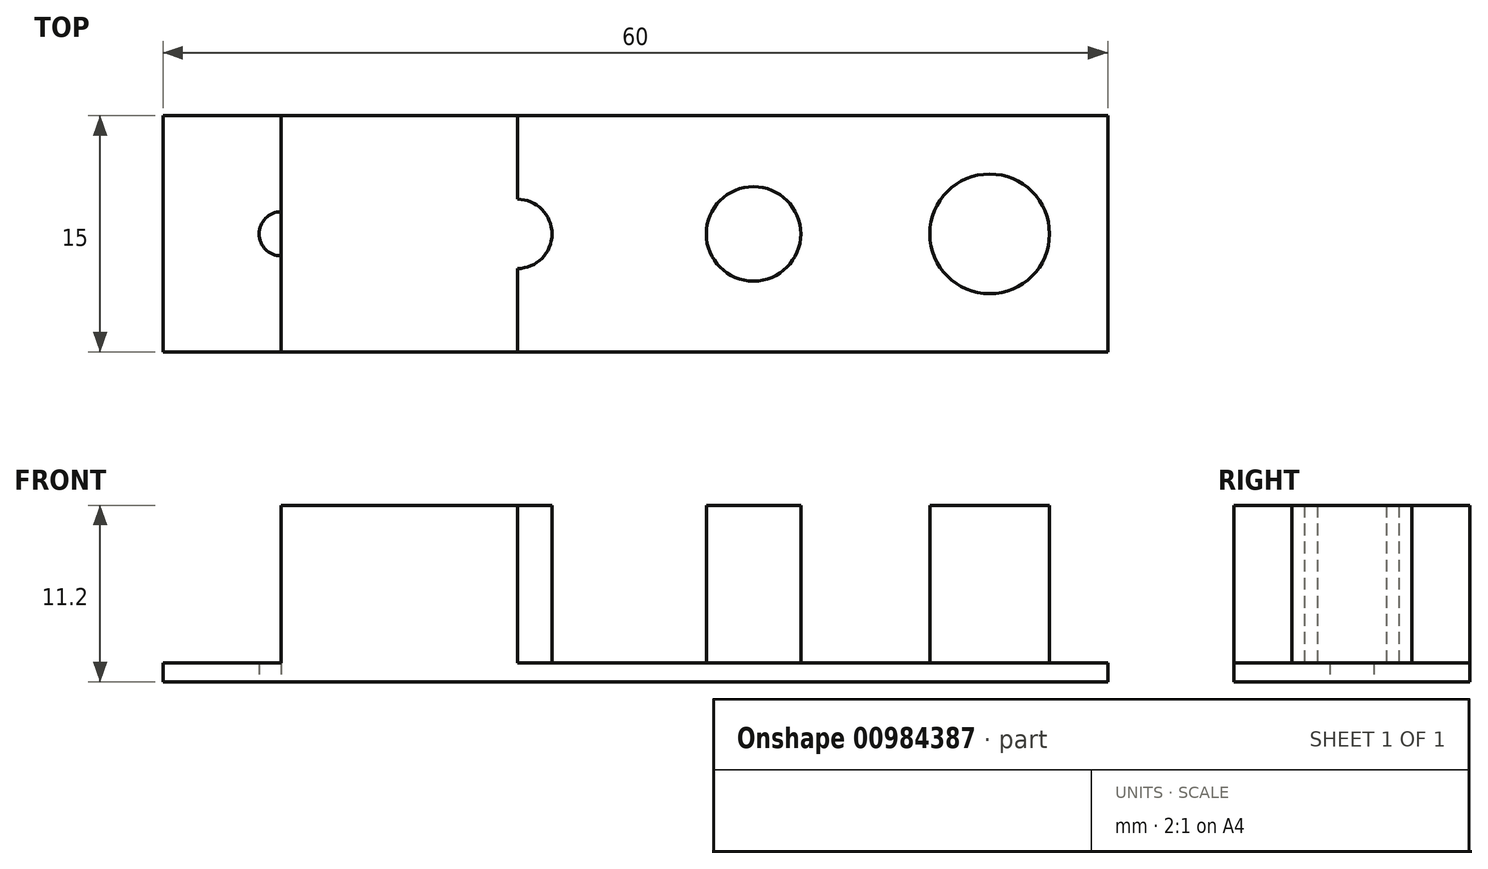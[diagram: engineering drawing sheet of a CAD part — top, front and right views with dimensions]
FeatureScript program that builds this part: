
annotation { "Feature Type Name" : "Feature", "Feature Type Description" : "" }
export const myFeature = defineFeature(function(context is Context, id is Id, definition is map)
    precondition{}
    {
        {
            var Q0;
            Q0=qCreatedBy(makeId("Top.planeOp"),FACE);
            var sketch = newSketch(context, id + "F0", { "sketchPlane" : qUnion([Q0])});
            skLineSegment(sketch, "E0.bottom", {"start": v(0, 0) * mm, "end": v(60, 0) * mm});
            skLineSegment(sketch, "E0.top", {"start": v(0, -15) * mm, "end": v(60, -15) * mm});
            skLineSegment(sketch, "E0.left", {"start": v(0, 0) * mm, "end": v(0, -15) * mm});
            skLineSegment(sketch, "E0.right", {"start": v(60, 0) * mm, "end": v(60, -15) * mm});
            skLineSegment(sketch, "E1.0", {"start": v(0, -7.5) * mm, "end": v(60, -7.5) * mm});
            skLineSegment(sketch, "E2.0", {"start": v(7.5, 0) * mm, "end": v(7.5, -30) * mm});
            skLineSegment(sketch, "E3.0", {"start": v(22.5, 0) * mm, "end": v(22.5, -30) * mm});
            skLineSegment(sketch, "E4.0", {"start": v(37.5, 0) * mm, "end": v(37.5, -30) * mm});
            skLineSegment(sketch, "E5.0", {"start": v(52.5, 0) * mm, "end": v(52.5, -30) * mm});
            skCircle(sketch, "E6", {"center": v(7.5, -7.5) * mm, "radius": 1.4 * mm});
            skCircle(sketch, "E7", {"center": v(22.5, -7.5) * mm, "radius": 2.2 * mm});
            skCircle(sketch, "E8", {"center": v(52.5, -7.5) * mm, "radius": 3.8 * mm});
            skCircle(sketch, "E9", {"center": v(37.5, -7.5) * mm, "radius": 3 * mm});
            skSolve(sketch);
        }
        {
            var Q0;
            {var subQ1=sQuery(id+"F0.wireOp",EDGE,"E0.bottom");var subQ6=sQuery(id+"F0.wireOp",EDGE,"E0.left");var subQ9=makeQuery(id+"F0.imprint","INTERSECT",VERTEX,{"derivedFrom":[subQ1,subQ6]});Q0=makeQuery(id+"F0.imprint","IMPRINT",FACE,{"disambiguationData":[TD([[makeQuery(id+"F0.imprint","IMPRINT",EDGE,{"disambiguationData":[TD([[subQ9,-1.0]])],"derivedFrom":subQ1}),-1.0]])]});}
            var Q1;
            {var subQ1=sQuery(id+"F0.wireOp",EDGE,"E0.left");var subQ5=sQuery(id+"F0.wireOp",EDGE,"E0.top");var subQ6=makeQuery(id+"F0.imprint","INTERSECT",VERTEX,{"derivedFrom":[subQ5,subQ1]});Q1=makeQuery(id+"F0.imprint","IMPRINT",FACE,{"disambiguationData":[TD([[makeQuery(id+"F0.imprint","IMPRINT",EDGE,{"disambiguationData":[TD([[subQ6,-1.0]])],"derivedFrom":subQ5}),1.0]])]});}
            var Q2;
            {var subQ1=sQuery(id+"F0.wireOp",EDGE,"E0.top");var subQ5=sQuery(id+"F0.wireOp",EDGE,"E2.0");var subQ6=makeQuery(id+"F0.imprint","INTERSECT",VERTEX,{"derivedFrom":[subQ1,subQ5]});Q2=makeQuery(id+"F0.imprint","IMPRINT",FACE,{"disambiguationData":[TD([[makeQuery(id+"F0.imprint","IMPRINT",EDGE,{"disambiguationData":[TD([[subQ6,-1.0]])],"derivedFrom":subQ1}),1.0]])]});}
            var Q3;
            {var subQ0=sQuery(id+"F0.wireOp",EDGE,"E2.0");var subQ1=sQuery(id+"F0.wireOp",EDGE,"E0.bottom");var subQ2=makeQuery(id+"F0.imprint","INTERSECT",VERTEX,{"derivedFrom":[subQ1,subQ0]});Q3=makeQuery(id+"F0.imprint","IMPRINT",FACE,{"disambiguationData":[TD([[makeQuery(id+"F0.imprint","IMPRINT",EDGE,{"disambiguationData":[TD([[subQ2,-1.0]])],"derivedFrom":subQ1}),-1.0]])]});}
            var Q4;
            {var subQ0=sQuery(id+"F0.wireOp",EDGE,"E3.0");var subQ1=sQuery(id+"F0.wireOp",EDGE,"E0.bottom");var subQ2=makeQuery(id+"F0.imprint","INTERSECT",VERTEX,{"derivedFrom":[subQ1,subQ0]});Q4=makeQuery(id+"F0.imprint","IMPRINT",FACE,{"disambiguationData":[TD([[makeQuery(id+"F0.imprint","IMPRINT",EDGE,{"disambiguationData":[TD([[subQ2,-1.0]])],"derivedFrom":subQ1}),-1.0]])]});}
            var Q5;
            {var subQ1=sQuery(id+"F0.wireOp",EDGE,"E0.top");var subQ5=sQuery(id+"F0.wireOp",EDGE,"E3.0");var subQ6=makeQuery(id+"F0.imprint","INTERSECT",VERTEX,{"derivedFrom":[subQ1,subQ5]});Q5=makeQuery(id+"F0.imprint","IMPRINT",FACE,{"disambiguationData":[TD([[makeQuery(id+"F0.imprint","IMPRINT",EDGE,{"disambiguationData":[TD([[subQ6,-1.0]])],"derivedFrom":subQ1}),1.0]])]});}
            var Q6;
            {var subQ1=sQuery(id+"F0.wireOp",EDGE,"E0.top");var subQ7=sQuery(id+"F0.wireOp",EDGE,"E4.0");var subQ8=makeQuery(id+"F0.imprint","INTERSECT",VERTEX,{"derivedFrom":[subQ1,subQ7]});Q6=makeQuery(id+"F0.imprint","IMPRINT",FACE,{"disambiguationData":[TD([[makeQuery(id+"F0.imprint","IMPRINT",EDGE,{"disambiguationData":[TD([[subQ8,-1.0]])],"derivedFrom":subQ1}),1.0]])]});}
            var Q7;
            {var subQ1=sQuery(id+"F0.wireOp",EDGE,"E0.bottom");var subQ5=sQuery(id+"F0.wireOp",EDGE,"E4.0");var subQ6=makeQuery(id+"F0.imprint","INTERSECT",VERTEX,{"derivedFrom":[subQ1,subQ5]});Q7=makeQuery(id+"F0.imprint","IMPRINT",FACE,{"disambiguationData":[TD([[makeQuery(id+"F0.imprint","IMPRINT",EDGE,{"disambiguationData":[TD([[subQ6,-1.0]])],"derivedFrom":subQ1}),-1.0]])]});}
            var Q8;
            {var subQ1=sQuery(id+"F0.wireOp",EDGE,"E0.right");var subQ5=sQuery(id+"F0.wireOp",EDGE,"E0.bottom");var subQ6=makeQuery(id+"F0.imprint","INTERSECT",VERTEX,{"derivedFrom":[subQ5,subQ1]});Q8=makeQuery(id+"F0.imprint","IMPRINT",FACE,{"disambiguationData":[TD([[makeQuery(id+"F0.imprint","IMPRINT",EDGE,{"disambiguationData":[TD([[subQ6,1.0]])],"derivedFrom":subQ5}),-1.0]])]});}
            var Q9;
            {var subQ1=sQuery(id+"F0.wireOp",EDGE,"E0.top");var subQ5=sQuery(id+"F0.wireOp",EDGE,"E0.right");var subQ6=makeQuery(id+"F0.imprint","INTERSECT",VERTEX,{"derivedFrom":[subQ1,subQ5]});Q9=makeQuery(id+"F0.imprint","IMPRINT",FACE,{"disambiguationData":[TD([[makeQuery(id+"F0.imprint","IMPRINT",EDGE,{"disambiguationData":[TD([[subQ6,1.0]])],"derivedFrom":subQ1}),1.0]])]});}
            extrude(context, id + "F1", {"entities" : qUnion([Q0, Q1, Q2, Q3, Q4, Q5, Q6, Q7, Q8, Q9]), "depth" : 1.2 * mm, "offsetDistance" : 25 * mm});
        }
        {
            var Q0;
            {var subQ0=sQuery(id+"F0.wireOp",EDGE,"E6");var subQ1=sQuery(id+"F0.wireOp",EDGE,"E1.0");var subQ2=makeQuery(id+"F0.imprint","INTERSECT",VERTEX,{"disambiguationData":[OD(0.0)],"derivedFrom":[subQ1,subQ0]});Q0=makeQuery(id+"F0.imprint","IMPRINT",FACE,{"disambiguationData":[TD([[makeQuery(id+"F0.imprint","IMPRINT",EDGE,{"disambiguationData":[TD([[subQ2,-1.0]])],"derivedFrom":subQ1}),1.0]])]});}
            var Q1;
            {var subQ0=sQuery(id+"F0.wireOp",EDGE,"E2.0");var subQ1=sQuery(id+"F0.wireOp",EDGE,"E1.0");var subQ2=makeQuery(id+"F0.imprint","INTERSECT",VERTEX,{"derivedFrom":[subQ1,subQ0]});Q1=makeQuery(id+"F0.imprint","IMPRINT",FACE,{"disambiguationData":[TD([[makeQuery(id+"F0.imprint","IMPRINT",EDGE,{"disambiguationData":[TD([[subQ2,-1.0]])],"derivedFrom":subQ1}),1.0]])]});}
            var Q2;
            {var subQ0=sQuery(id+"F0.wireOp",EDGE,"E2.0");var subQ1=sQuery(id+"F0.wireOp",EDGE,"E1.0");var subQ2=makeQuery(id+"F0.imprint","INTERSECT",VERTEX,{"derivedFrom":[subQ1,subQ0]});Q2=makeQuery(id+"F0.imprint","IMPRINT",FACE,{"disambiguationData":[TD([[makeQuery(id+"F0.imprint","IMPRINT",EDGE,{"disambiguationData":[TD([[subQ2,-1.0]])],"derivedFrom":subQ1}),-1.0]])]});}
            var Q3;
            {var subQ0=sQuery(id+"F0.wireOp",EDGE,"E6");var subQ1=sQuery(id+"F0.wireOp",EDGE,"E1.0");var subQ2=makeQuery(id+"F0.imprint","INTERSECT",VERTEX,{"disambiguationData":[OD(0.0)],"derivedFrom":[subQ1,subQ0]});Q3=makeQuery(id+"F0.imprint","IMPRINT",FACE,{"disambiguationData":[TD([[makeQuery(id+"F0.imprint","IMPRINT",EDGE,{"disambiguationData":[TD([[subQ2,-1.0]])],"derivedFrom":subQ1}),-1.0]])]});}
            var Q4;
            {var subQ0=sQuery(id+"F0.wireOp",EDGE,"E7");var subQ1=sQuery(id+"F0.wireOp",EDGE,"E1.0");var subQ2=makeQuery(id+"F0.imprint","INTERSECT",VERTEX,{"disambiguationData":[OD(0.0)],"derivedFrom":[subQ1,subQ0]});Q4=makeQuery(id+"F0.imprint","IMPRINT",FACE,{"disambiguationData":[TD([[makeQuery(id+"F0.imprint","IMPRINT",EDGE,{"disambiguationData":[TD([[subQ2,-1.0]])],"derivedFrom":subQ1}),-1.0]])]});}
            var Q5;
            {var subQ0=sQuery(id+"F0.wireOp",EDGE,"E7");var subQ1=sQuery(id+"F0.wireOp",EDGE,"E1.0");var subQ2=makeQuery(id+"F0.imprint","INTERSECT",VERTEX,{"disambiguationData":[OD(0.0)],"derivedFrom":[subQ1,subQ0]});Q5=makeQuery(id+"F0.imprint","IMPRINT",FACE,{"disambiguationData":[TD([[makeQuery(id+"F0.imprint","IMPRINT",EDGE,{"disambiguationData":[TD([[subQ2,-1.0]])],"derivedFrom":subQ1}),1.0]])]});}
            var Q6;
            {var subQ0=sQuery(id+"F0.wireOp",EDGE,"E3.0");var subQ1=sQuery(id+"F0.wireOp",EDGE,"E1.0");var subQ2=makeQuery(id+"F0.imprint","INTERSECT",VERTEX,{"derivedFrom":[subQ1,subQ0]});Q6=makeQuery(id+"F0.imprint","IMPRINT",FACE,{"disambiguationData":[TD([[makeQuery(id+"F0.imprint","IMPRINT",EDGE,{"disambiguationData":[TD([[subQ2,-1.0]])],"derivedFrom":subQ1}),1.0]])]});}
            var Q7;
            {var subQ0=sQuery(id+"F0.wireOp",EDGE,"E3.0");var subQ1=sQuery(id+"F0.wireOp",EDGE,"E1.0");var subQ2=makeQuery(id+"F0.imprint","INTERSECT",VERTEX,{"derivedFrom":[subQ1,subQ0]});Q7=makeQuery(id+"F0.imprint","IMPRINT",FACE,{"disambiguationData":[TD([[makeQuery(id+"F0.imprint","IMPRINT",EDGE,{"disambiguationData":[TD([[subQ2,-1.0]])],"derivedFrom":subQ1}),-1.0]])]});}
            var Q8;
            {var subQ0=sQuery(id+"F0.wireOp",EDGE,"E4.0");var subQ1=sQuery(id+"F0.wireOp",EDGE,"E1.0");var subQ2=makeQuery(id+"F0.imprint","INTERSECT",VERTEX,{"derivedFrom":[subQ1,subQ0]});Q8=makeQuery(id+"F0.imprint","IMPRINT",FACE,{"disambiguationData":[TD([[makeQuery(id+"F0.imprint","IMPRINT",EDGE,{"disambiguationData":[TD([[subQ2,-1.0]])],"derivedFrom":subQ1}),1.0]])]});}
            var Q9;
            {var subQ0=sQuery(id+"F0.wireOp",EDGE,"E9");var subQ1=sQuery(id+"F0.wireOp",EDGE,"E1.0");var subQ2=makeQuery(id+"F0.imprint","INTERSECT",VERTEX,{"disambiguationData":[OD(0.0)],"derivedFrom":[subQ1,subQ0]});Q9=makeQuery(id+"F0.imprint","IMPRINT",FACE,{"disambiguationData":[TD([[makeQuery(id+"F0.imprint","IMPRINT",EDGE,{"disambiguationData":[TD([[subQ2,-1.0]])],"derivedFrom":subQ1}),1.0]])]});}
            var Q10;
            {var subQ0=sQuery(id+"F0.wireOp",EDGE,"E9");var subQ1=sQuery(id+"F0.wireOp",EDGE,"E1.0");var subQ2=makeQuery(id+"F0.imprint","INTERSECT",VERTEX,{"disambiguationData":[OD(0.0)],"derivedFrom":[subQ1,subQ0]});Q10=makeQuery(id+"F0.imprint","IMPRINT",FACE,{"disambiguationData":[TD([[makeQuery(id+"F0.imprint","IMPRINT",EDGE,{"disambiguationData":[TD([[subQ2,-1.0]])],"derivedFrom":subQ1}),-1.0]])]});}
            var Q11;
            {var subQ0=sQuery(id+"F0.wireOp",EDGE,"E4.0");var subQ1=sQuery(id+"F0.wireOp",EDGE,"E1.0");var subQ2=makeQuery(id+"F0.imprint","INTERSECT",VERTEX,{"derivedFrom":[subQ1,subQ0]});Q11=makeQuery(id+"F0.imprint","IMPRINT",FACE,{"disambiguationData":[TD([[makeQuery(id+"F0.imprint","IMPRINT",EDGE,{"disambiguationData":[TD([[subQ2,-1.0]])],"derivedFrom":subQ1}),-1.0]])]});}
            var Q12;
            {var subQ0=sQuery(id+"F0.wireOp",EDGE,"E8");var subQ1=sQuery(id+"F0.wireOp",EDGE,"E1.0");var subQ2=makeQuery(id+"F0.imprint","INTERSECT",VERTEX,{"disambiguationData":[OD(0.0)],"derivedFrom":[subQ1,subQ0]});Q12=makeQuery(id+"F0.imprint","IMPRINT",FACE,{"disambiguationData":[TD([[makeQuery(id+"F0.imprint","IMPRINT",EDGE,{"disambiguationData":[TD([[subQ2,-1.0]])],"derivedFrom":subQ1}),-1.0]])]});}
            var Q13;
            {var subQ0=sQuery(id+"F0.wireOp",EDGE,"E8");var subQ1=sQuery(id+"F0.wireOp",EDGE,"E1.0");var subQ2=makeQuery(id+"F0.imprint","INTERSECT",VERTEX,{"disambiguationData":[OD(0.0)],"derivedFrom":[subQ1,subQ0]});Q13=makeQuery(id+"F0.imprint","IMPRINT",FACE,{"disambiguationData":[TD([[makeQuery(id+"F0.imprint","IMPRINT",EDGE,{"disambiguationData":[TD([[subQ2,-1.0]])],"derivedFrom":subQ1}),1.0]])]});}
            var Q14;
            {var subQ0=sQuery(id+"F0.wireOp",EDGE,"E5.0");var subQ1=sQuery(id+"F0.wireOp",EDGE,"E1.0");var subQ2=makeQuery(id+"F0.imprint","INTERSECT",VERTEX,{"derivedFrom":[subQ1,subQ0]});Q14=makeQuery(id+"F0.imprint","IMPRINT",FACE,{"disambiguationData":[TD([[makeQuery(id+"F0.imprint","IMPRINT",EDGE,{"disambiguationData":[TD([[subQ2,-1.0]])],"derivedFrom":subQ1}),1.0]])]});}
            var Q15;
            {var subQ0=sQuery(id+"F0.wireOp",EDGE,"E5.0");var subQ1=sQuery(id+"F0.wireOp",EDGE,"E1.0");var subQ2=makeQuery(id+"F0.imprint","INTERSECT",VERTEX,{"derivedFrom":[subQ1,subQ0]});Q15=makeQuery(id+"F0.imprint","IMPRINT",FACE,{"disambiguationData":[TD([[makeQuery(id+"F0.imprint","IMPRINT",EDGE,{"disambiguationData":[TD([[subQ2,-1.0]])],"derivedFrom":subQ1}),-1.0]])]});}
            extrude(context, id + "F2", {"entities" : qUnion([Q0, Q1, Q2, Q3, Q4, Q5, Q6, Q7, Q8, Q9, Q10, Q11, Q12, Q13, Q14, Q15]), "operationType" : NewBodyOperationType.ADD, "depth" : 11.2 * mm, "offsetDistance" : 25 * mm});
        }
    });
